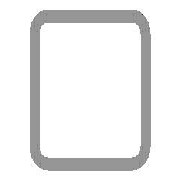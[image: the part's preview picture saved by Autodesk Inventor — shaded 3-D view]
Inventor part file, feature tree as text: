
AUTODESK INVENTOR PART (.ipt)
format: ipt  version: 2023 (Build 270158000, 158)  size: 193,536 bytes
history: native  units: mm (DEFAULTED — no unit token found)
features: other x9, sketch x4, extrude x2, plane x1
ambient origin geometry x8: Origin, YZ Plane, XZ Plane, XY Plane, X Axis, Y Axis, Z Axis, Center Point
bodies: Solid1 (feature_tree)
feature tree (16):
  parser-record x1  (decoder bookkeeping rows leaked as tree rows — omitted from the tree; the rows remain in map.json)
  other  "Driven Length"
  other  "Płaszczyzna początkowa"
  other  "Płaszczyzna końcowa"
  extrude  "Bryła"  TaperAngle=0.0deg  [1 undecoded]
  other  "Płaszczyzna konstrukcyjna4"
  other  "Płaszczyzna konstrukcyjna5"
  other  "Płaszczyzna konstrukcyjna6"
  extrude  "Wyciągnięcie proste2"  Depth=4.0mm
  other  "Utwórz kombinację1"
  sketch  "Szkic"
  sketch  "Sketch3"  dims[d3=800.0mm d4=0.0mm]
  plane  "Work Plane3"
  sketch  "Sketch4"  dims[d7=4.0mm d10=40.0mm d11=40.0mm d12=3.2mm d13=-0.0mm d14=800.0mm d15=20.0mm d16=20.0mm d17=90.0deg d18=800.0mm d19=0.13mm d20=0.0mm]
  sketch  "Szkic5"
  other  "Bryła2"
note: 1 required parameter value undecoded (feature->parameter linkage not recoverable at this tier; creation-order binding heuristic only, values carry confidence <= 0.55)
